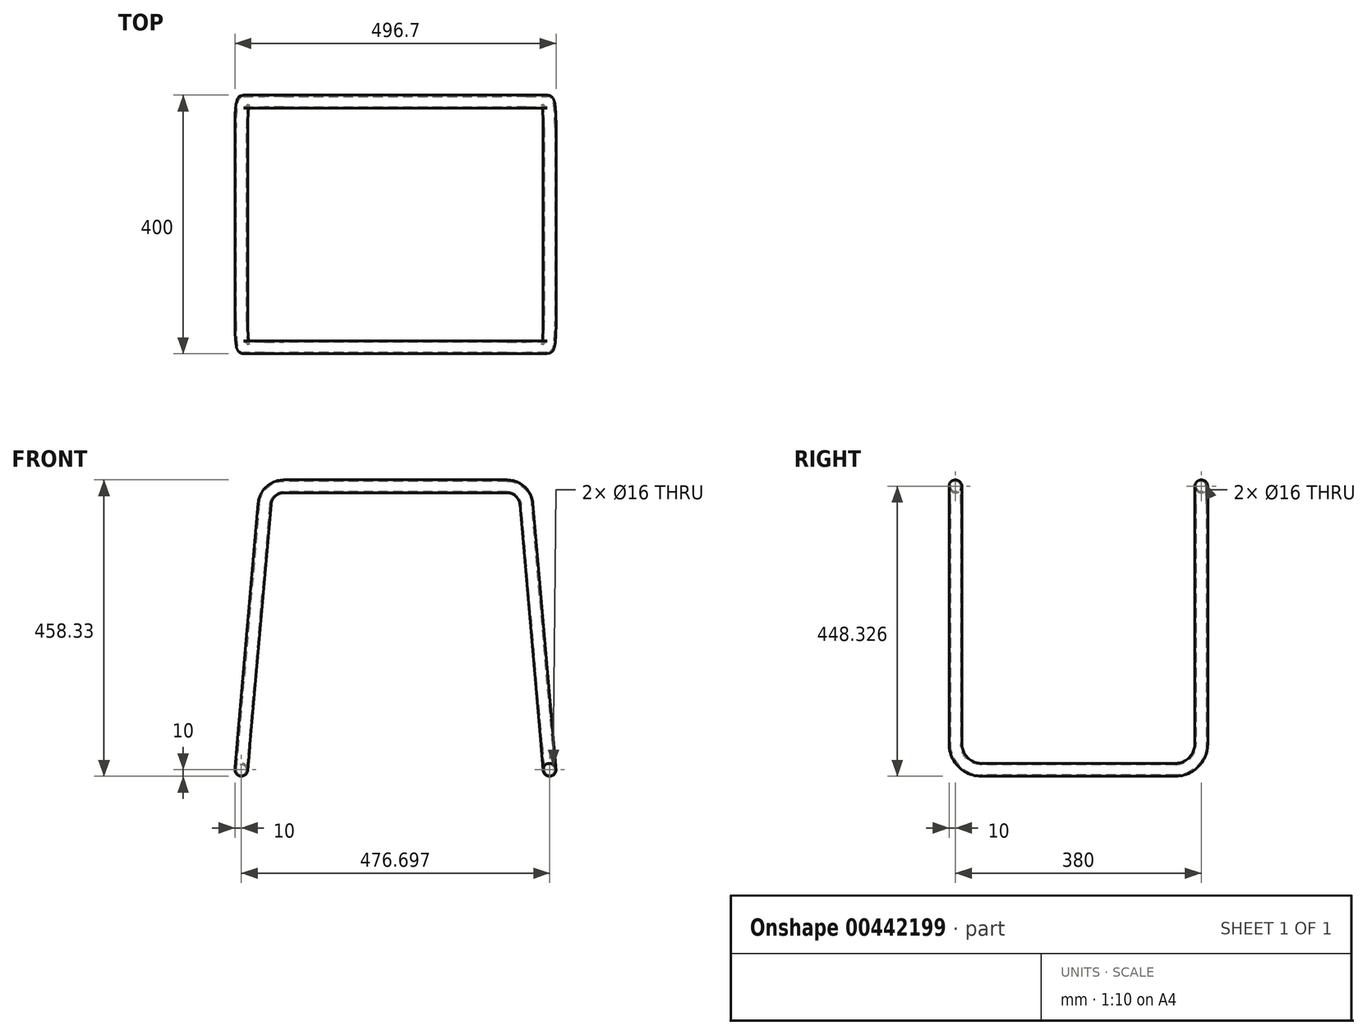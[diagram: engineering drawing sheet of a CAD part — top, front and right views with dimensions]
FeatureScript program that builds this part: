
annotation { "Feature Type Name" : "Feature", "Feature Type Description" : "" }
export const myFeature = defineFeature(function(context is Context, id is Id, definition is map)
    precondition{}
    {
        {
            var Q0;
            Q0=qCreatedBy(makeId("Front.planeOp"),FACE);
            var sketch = newSketch(context, id + "F0", { "sketchPlane" : qUnion([Q0])});
            skLineSegment(sketch, "E0", {"start": v(476.7, 0) * mm, "end": v(440.74, 410.94) * mm, "construction": true});
            skLineSegment(sketch, "E1", {"start": v(410.86, 438.33) * mm, "end": v(65.84, 438.33) * mm});
            skLineSegment(sketch, "E2", {"start": v(35.95, 410.94) * mm, "end": v(0, 0) * mm, "construction": true});
            skPoint(sketch, "E3.visualSharp", {"position": v(38.35, 438.33) * mm});
            skArc(sketch, "E3.filletArc", {"start": v(65.84, 438.33) * mm, "mid": v(45.57, 430.44) * mm, "end": v(35.95, 410.94) * mm});
            skPoint(sketch, "E4.visualSharp", {"position": v(438.35, 438.33) * mm});
            skArc(sketch, "E4.filletArc", {"start": v(440.74, 410.94) * mm, "mid": v(431.13, 430.44) * mm, "end": v(410.86, 438.33) * mm});
            skSolve(sketch);
        }
        {
            var Q0;
            Q0=qCreatedBy(makeId("Top.planeOp"),FACE);
            var sketch = newSketch(context, id + "F1", { "sketchPlane" : qUnion([Q0])});
            skLineSegment(sketch, "E5", {"start": v(0, 0) * mm, "end": v(0, 380) * mm, "construction": true});
            skLineSegment(sketch, "E6", {"start": v(476.7, 0) * mm, "end": v(476.7, 380) * mm, "construction": true});
            skLineSegment(sketch, "E7", {"start": v(0, 190) * mm, "end": v(476.7, 190) * mm, "construction": true});
            skLineSegment(sketch, "E8", {"start": v(0, 380) * mm, "end": v(476.7, 380) * mm, "construction": true});
            skLineSegment(sketch, "E9", {"start": v(0, 0) * mm, "end": v(476.7, 0) * mm, "construction": true});
            skSolve(sketch);
        }
        {
            var Q0;
            Q0=qCreatedBy(makeId("Front.planeOp"),FACE);
            var Q1;
            Q1=sQuery(id+"F1.wireOp",VERTEX,"E5.end");
            cPlane(context, id + "F2", {"entities" : qUnion([Q0, Q1]), "cplaneType" : CPlaneType.PLANE_POINT, "offset" : 25 * mm, "width" : 150 * mm, "height" : 150 * mm});
        }
        {
            var Q0;
            Q0=qCreatedBy(id+"F2.planeOp",FACE);
            var sketch = newSketch(context, id + "F3", { "sketchPlane" : qUnion([Q0])});
            skLineSegment(sketch, "E10", {"start": v(476.7, 0) * mm, "end": v(440.74, 410.94) * mm, "construction": true});
            skLineSegment(sketch, "E11", {"start": v(410.86, 438.33) * mm, "end": v(65.84, 438.33) * mm});
            skLineSegment(sketch, "E12", {"start": v(35.95, 410.94) * mm, "end": v(0, 0) * mm, "construction": true});
            skPoint(sketch, "E13.visualSharp", {"position": v(38.35, 438.33) * mm});
            skArc(sketch, "E13.filletArc", {"start": v(65.84, 438.33) * mm, "mid": v(45.57, 430.44) * mm, "end": v(35.95, 410.94) * mm});
            skPoint(sketch, "E14.visualSharp", {"position": v(438.35, 438.33) * mm});
            skArc(sketch, "E14.filletArc", {"start": v(440.74, 410.94) * mm, "mid": v(431.13, 430.44) * mm, "end": v(410.86, 438.33) * mm});
            skSolve(sketch);
        }
        {
            var Q0;
            Q0=sQuery(id+"F0.wireOp",EDGE,"E0");
            cPlane(context, id + "F4", {"entities" : qUnion([Q0]), "cplaneType" : CPlaneType.LINE_ANGLE, "offset" : 25 * mm, "angle" : 0 * degree, "width" : 150 * mm, "height" : 150 * mm});
        }
        {
            var Q0;
            Q0=sQuery(id+"F0.wireOp",EDGE,"E2");
            var Q1;
            Q1=sQuery(id+"F1.wireOp",EDGE,"E5");
            cPlane(context, id + "F5", {"entities" : qUnion([Q0, Q1]), "cplaneType" : CPlaneType.LINE_ANGLE, "offset" : 25 * mm, "angle" : 0 * degree, "width" : 150 * mm, "height" : 150 * mm});
        }
        {
            var Q0;
            Q0=qCreatedBy(id+"F4.planeOp",FACE);
            var sketch = newSketch(context, id + "F6", { "sketchPlane" : qUnion([Q0])});
            skLineSegment(sketch, "E15", {"start": v(40, -41.55) * mm, "end": v(340, -41.55) * mm});
            skLineSegment(sketch, "E16", {"start": v(0, -1.55) * mm, "end": v(0, 370.96) * mm});
            skLineSegment(sketch, "E17", {"start": v(380, -1.55) * mm, "end": v(380, 370.96) * mm});
            skPoint(sketch, "E18.visualSharp", {"position": v(0, -41.55) * mm});
            skArc(sketch, "E18.filletArc", {"start": v(0, -1.55) * mm, "mid": v(11.72, -29.83) * mm, "end": v(40, -41.55) * mm});
            skPoint(sketch, "E19.visualSharp", {"position": v(380, -41.55) * mm});
            skArc(sketch, "E19.filletArc", {"start": v(340, -41.55) * mm, "mid": v(368.28, -29.83) * mm, "end": v(380, -1.55) * mm});
            skSolve(sketch);
        }
        {
            var Q0;
            Q0=qCreatedBy(id+"F5.planeOp",FACE);
            var sketch = newSketch(context, id + "F7", { "sketchPlane" : qUnion([Q0])});
            skLineSegment(sketch, "E20", {"start": v(40, 0) * mm, "end": v(340, 0) * mm});
            skLineSegment(sketch, "E21", {"start": v(0, 40) * mm, "end": v(0, 412.51) * mm});
            skLineSegment(sketch, "E22", {"start": v(380, 40) * mm, "end": v(380, 412.51) * mm});
            skArc(sketch, "E23.filletArc", {"start": v(0, 40) * mm, "mid": v(11.72, 11.72) * mm, "end": v(40, 0) * mm});
            skArc(sketch, "E24.filletArc", {"start": v(340, 0) * mm, "mid": v(368.28, 11.72) * mm, "end": v(380, 40) * mm});
            skSolve(sketch);
        }
        {
            var Q0;
            Q0=qCreatedBy(makeId("Front.planeOp"),FACE);
            cPlane(context, id + "F8", {"entities" : qUnion([Q0]), "cplaneType" : CPlaneType.OFFSET, "offset" : 40 * mm, "oppositeDirection" : true, "width" : 150 * mm, "height" : 150 * mm});
        }
        {
            var Q0;
            Q0=qCreatedBy(id+"F8.planeOp",FACE);
            var sketch = newSketch(context, id + "F9", { "sketchPlane" : qUnion([Q0])});
            skCircle(sketch, "E25", {"center": v(0, 0) * mm, "radius": 10 * mm});
            skCircle(sketch, "E26", {"center": v(0, 0) * mm, "radius": 8 * mm});
            skSolve(sketch);
        }
        {
            var Q0;
            Q0=makeQuery(id+"F9.imprint","IMPRINT",FACE,{"disambiguationData":[TD([[makeQuery(id+"F9.imprint","IMPRINT",EDGE,{"derivedFrom":sQuery(id+"F9.wireOp",EDGE,"E25")}),1.0]])]});
            var Q1;
            Q1=sQuery(id+"F7.wireOp",EDGE,"E20");
            var Q2;
            Q2=sQuery(id+"F7.wireOp",EDGE,"E24.filletArc");
            var Q3;
            Q3=sQuery(id+"F7.wireOp",EDGE,"E22");
            var Q4;
            Q4=sQuery(id+"F3.wireOp",EDGE,"E13.filletArc");
            var Q5;
            Q5=sQuery(id+"F3.wireOp",EDGE,"E11");
            var Q6;
            Q6=sQuery(id+"F3.wireOp",EDGE,"E14.filletArc");
            var Q7;
            Q7=sQuery(id+"F6.wireOp",EDGE,"E17");
            var Q8;
            Q8=sQuery(id+"F6.wireOp",EDGE,"E19.filletArc");
            var Q9;
            Q9=sQuery(id+"F6.wireOp",EDGE,"E15");
            var Q10;
            Q10=sQuery(id+"F6.wireOp",EDGE,"E18.filletArc");
            var Q11;
            Q11=sQuery(id+"F6.wireOp",EDGE,"E16");
            var Q12;
            Q12=sQuery(id+"F0.wireOp",EDGE,"E4.filletArc");
            var Q13;
            Q13=sQuery(id+"F0.wireOp",EDGE,"E1");
            var Q14;
            Q14=sQuery(id+"F0.wireOp",EDGE,"E3.filletArc");
            var Q15;
            Q15=sQuery(id+"F7.wireOp",EDGE,"E21");
            var Q16;
            Q16=sQuery(id+"F7.wireOp",EDGE,"E23.filletArc");
            sweep(context, id + "F10", {"profiles" : qUnion([Q0]), "path" : qUnion([Q1, Q2, Q3, Q4, Q5, Q6, Q7, Q8, Q9, Q10, Q11, Q12, Q13, Q14, Q15, Q16])});
        }
    });
